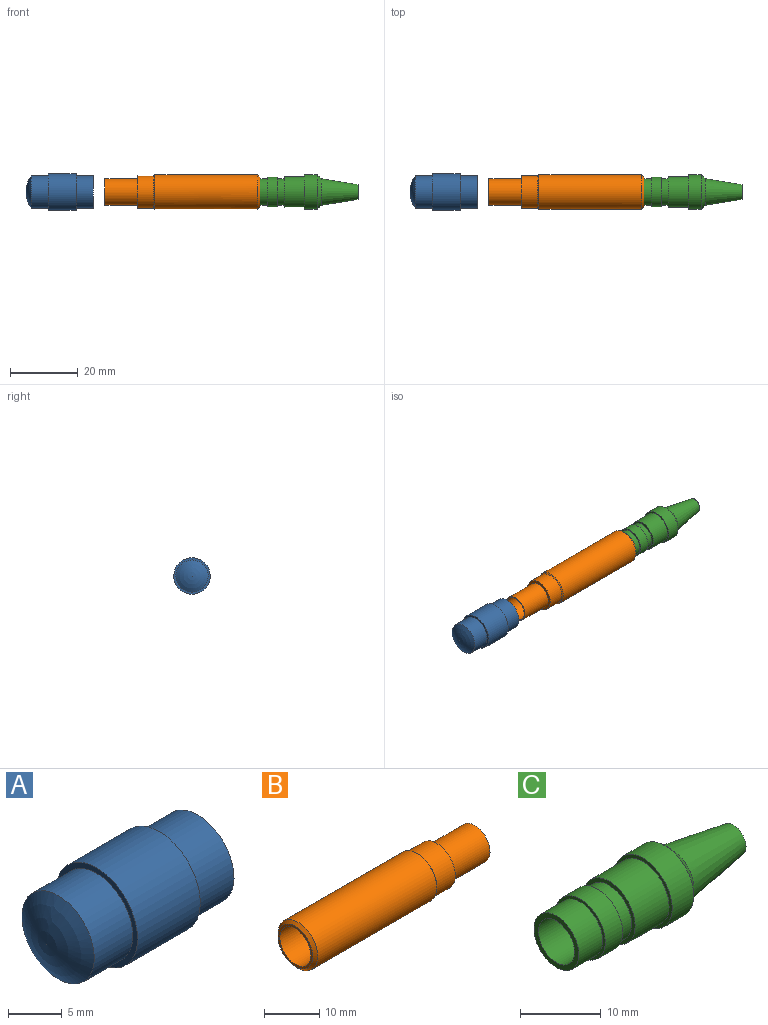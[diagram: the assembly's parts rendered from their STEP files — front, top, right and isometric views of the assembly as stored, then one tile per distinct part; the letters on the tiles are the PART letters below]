
ASSEMBLY  parts=3 mates=2
PART A: 11 faces, bbox 19.9x10.8x10.8 mm
  f0: cylinder r=4.76mm len=9.53mm, axis (-1,0,0), area 152mm2, adj f1,f8
  f1: sphere r=8.2mm, area 78.6mm2, adj f0
  f2: plane 8.89x8.89mm, normal (1,0,0), area 6.2mm2, adj f3,f10
  f3: cylinder r=4.45mm len=8.89mm, axis (-1,0,0), area 223.5mm2, adj f2,f4
  f4: plane 9.53x9.53mm, normal (1,0,0), area 9.2mm2, adj f3,f5
  f5: cylinder r=4.76mm len=9.53mm, axis (-1,0,0), area 152mm2, adj f4,f6
  f6: plane 10.8x10.8mm, normal (1,0,0), area 20.3mm2, adj f5,f7
  f7: cylinder r=5.4mm len=10.8mm, axis (-1,0,0), area 280mm2, adj f6,f8
  f8: plane 10.8x10.8mm, normal (-1,0,0), area 20.3mm2, adj f0,f7
  f9: cone r=0mm half-angle=59deg, axis (1,0,0), area 65.2mm2, adj f10
  f10: cylinder r=4.22mm len=9.27mm, axis (1,0,0), area 245.6mm2, adj f2,f9
PART B: 12 faces, bbox 45.9x10.2x10.2 mm
  f0: cone r=0mm half-angle=59deg, axis (1,0,0), area 36.8mm2, adj f7,f8
  f1: cylinder r=5.08mm len=30.48mm, axis (-1,0,0), area 972.9mm2, adj f10,f11
  f2: plane 8.89x8.89mm, normal (-1,0,0), area 12.6mm2, adj f9,f11
  f3: plane 7.81x7.81mm, normal (1,0,0), area 7.8mm2, adj f4,f7
  f4: cylinder r=3.9mm len=9.71mm, axis (-1,0,0), area 238.1mm2, adj f3,f5
  f5: plane 9.53x9.53mm, normal (1,0,0), area 23.4mm2, adj f4,f6
  f6: cylinder r=4.76mm len=9.53mm, axis (-1,0,0), area 143mm2, adj f5,f10
  f7: cylinder r=3.57mm len=32.51mm, axis (1,0,0), area 729.7mm2, adj f0,f3
  f8: cone r=0mm half-angle=59deg, axis (-1,0,0), area 47.8mm2, adj f0,f9
  f9: cylinder r=3.97mm len=10.86mm, axis (-1,0,0), area 270.8mm2, adj f2,f8
  f10: cone r=5.08mm half-angle=45deg, axis (-1,0,0), area 13.9mm2, adj f1,f6
  f11: cone r=4.45mm half-angle=45deg, axis (1,0,0), area 26.9mm2, adj f1,f2
PART C: 16 faces, bbox 31.1x10.2x10.2 mm
  f0: plane 7.87x7.87mm, normal (-1,0,0), area 17mm2, adj f1,f15
  f1: cylinder r=3.17mm len=22.23mm, axis (-1,0,0), area 443.4mm2, adj f0,f2
  f2: plane 6.35x6.35mm, normal (-1,0,0), area 21.7mm2, adj f1,f3
  f3: cylinder r=1.78mm len=8.89mm, axis (-1,0,0), area 99.3mm2, adj f2,f4
  f4: plane 4.36x4.36mm, normal (1,0,0), area 5mm2, adj f3,f5
  f5: cone r=3.94mm half-angle=9.1deg, axis (-1,0,0), area 212.5mm2, adj f4,f6
  f6: cone r=5.08mm half-angle=45deg, axis (-1,0,0), area 45.8mm2, adj f5,f7
  f7: cylinder r=5.08mm len=10.16mm, axis (-1,0,0), area 121.6mm2, adj f6,f8
  f8: plane 10.16x10.16mm, normal (-1,0,0), area 16.1mm2, adj f7,f9
  f9: cylinder r=4.55mm len=9.09mm, axis (-1,0,0), area 170.5mm2, adj f8,f10
  f10: plane 9.09x9.09mm, normal (-1,0,0), area 16.2mm2, adj f9,f11
  f11: cylinder r=3.94mm len=7.87mm, axis (-1,0,0), area 50.3mm2, adj f10,f12
  f12: plane 8.76x8.76mm, normal (1,0,0), area 11.6mm2, adj f11,f13
  f13: cylinder r=4.38mm len=8.76mm, axis (-1,0,0), area 83.9mm2, adj f12,f14
  f14: plane 8.76x8.76mm, normal (-1,0,0), area 11.6mm2, adj f13,f15
  f15: cylinder r=3.94mm len=7.87mm, axis (-1,0,0), area 103.7mm2, adj f0,f14
PLACE A t=(-35.35,21.87,0)mm
PLACE B rot(axis=(0,1,0),180deg) t=(33.93,21.87,0)mm
PLACE C t=(31.83,21.87,0)mm
MATE cylindrical B.f0 <-> A.f0  axis (1,0,0) through (-7.14,21.87,0)mm
MATE cylindrical B.f0 <-> C.f1  axis (1,0,0) through (33.93,21.87,0)mm
